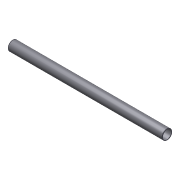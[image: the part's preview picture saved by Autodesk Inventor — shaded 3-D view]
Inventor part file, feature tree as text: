
AUTODESK INVENTOR PART (.ipt)
format: ipt  version: 2012 (Build 160160000, 160)  size: 101,888 bytes
history: native  units: in
note: dims shown in document units (in); Inventor stores cm internally (conversion verified against a paired STEP export)
features: other x42, revolve x1, sketch x1
ambient origin geometry x8: Origin, YZ Plane, XZ Plane, XY Plane, X Axis, Y Axis, Z Axis, Center Point
bodies: Solid1 (feature_tree)
feature tree (44):
  revolve  "Revolution1"  [1 undecoded]
  other  "tube_front_XY"
  other  "tube_front_YZ"
  other  "tube_front_ZX"
  other  "tube_front_X"
  other  "tube_front_Y"
  other  "tube_front_Z"
  other  "tube_front_Center"
  other  "tube_rear_XY"
  other  "tube_rear_YZ"
  other  "tube_rear_ZX"
  other  "tube_rear_X"
  other  "tube_rear_Y"
  other  "tube_rear_Z"
  other  "tube_rear_Center"
  other  "cp1_XY"
  other  "cp1_YZ"
  other  "cp1_ZX"
  other  "cp1_X"
  other  "cp1_Y"
  other  "cp1_Z"
  other  "cp1_Center"
  other  "cp2_XY"
  other  "cp2_YZ"
  other  "cp2_ZX"
  other  "cp2_X"
  other  "cp2_Y"
  other  "cp2_Z"
  other  "cp2_Center"
  other  "cp3_XY"
  other  "cp3_YZ"
  other  "cp3_ZX"
  other  "cp3_X"
  other  "cp3_Y"
  other  "cp3_Z"
  other  "cp3_Center"
  other  "cp4_XY"
  other  "cp4_YZ"
  other  "cp4_ZX"
  other  "cp4_X"
  other  "cp4_Y"
  other  "cp4_Z"
  other  "cp4_Center"
  sketch  "Sketch_1"  dims[d0=360.0deg]
note: 1 required parameter value undecoded (feature->parameter linkage not recoverable at this tier; creation-order binding heuristic only, values carry confidence <= 0.55)
